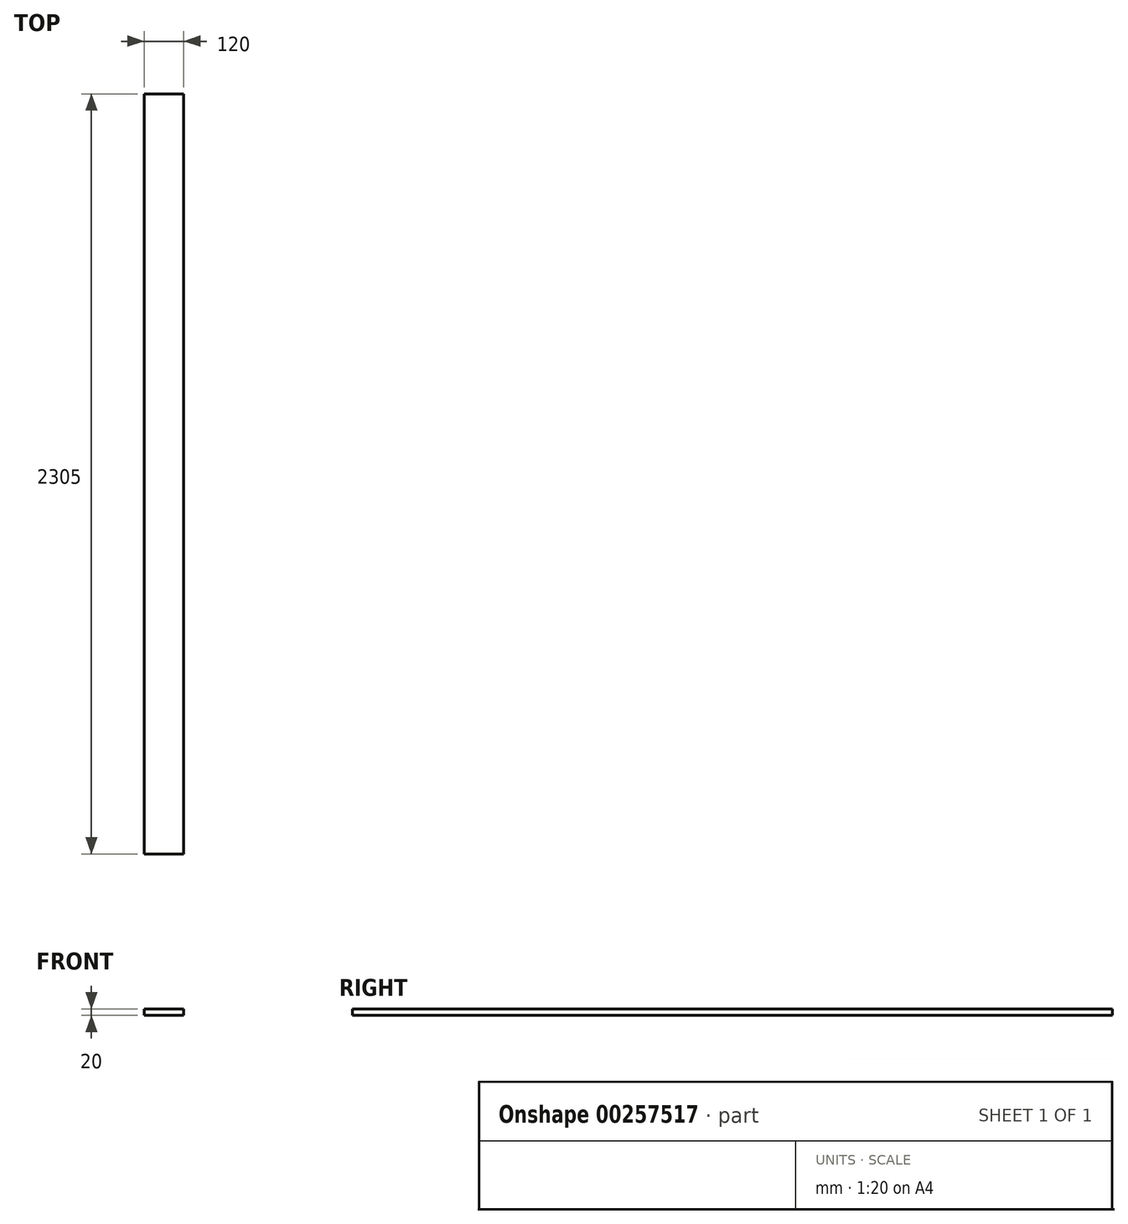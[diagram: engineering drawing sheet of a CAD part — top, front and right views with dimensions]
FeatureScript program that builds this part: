
annotation { "Feature Type Name" : "Feature", "Feature Type Description" : "" }
export const myFeature = defineFeature(function(context is Context, id is Id, definition is map)
    precondition{}
    {
        {
            var Q0;
            Q0=qCreatedBy(makeId("Front.planeOp"),FACE);
            var sketch = newSketch(context, id + "F0", { "sketchPlane" : qUnion([Q0])});
            skLineSegment(sketch, "E0.bottom", {"start": v(0, 0) * mm, "end": v(120, 0) * mm});
            skLineSegment(sketch, "E0.top", {"start": v(0, 20) * mm, "end": v(120, 20) * mm});
            skLineSegment(sketch, "E0.left", {"start": v(0, 0) * mm, "end": v(0, 20) * mm});
            skLineSegment(sketch, "E0.right", {"start": v(120, 0) * mm, "end": v(120, 20) * mm});
            skSolve(sketch);
        }
        {
            var Q0;
            Q0=makeQuery(id+"F0.imprint","IMPRINT",FACE,{"disambiguationData":[TD([[makeQuery(id+"F0.imprint","IMPRINT",EDGE,{"derivedFrom":sQuery(id+"F0.wireOp",EDGE,"E0.bottom")}),1.0]])]});
            extrude(context, id + "F1", {"entities" : qUnion([Q0]), "depth" : 2305 * mm});
        }
    });
